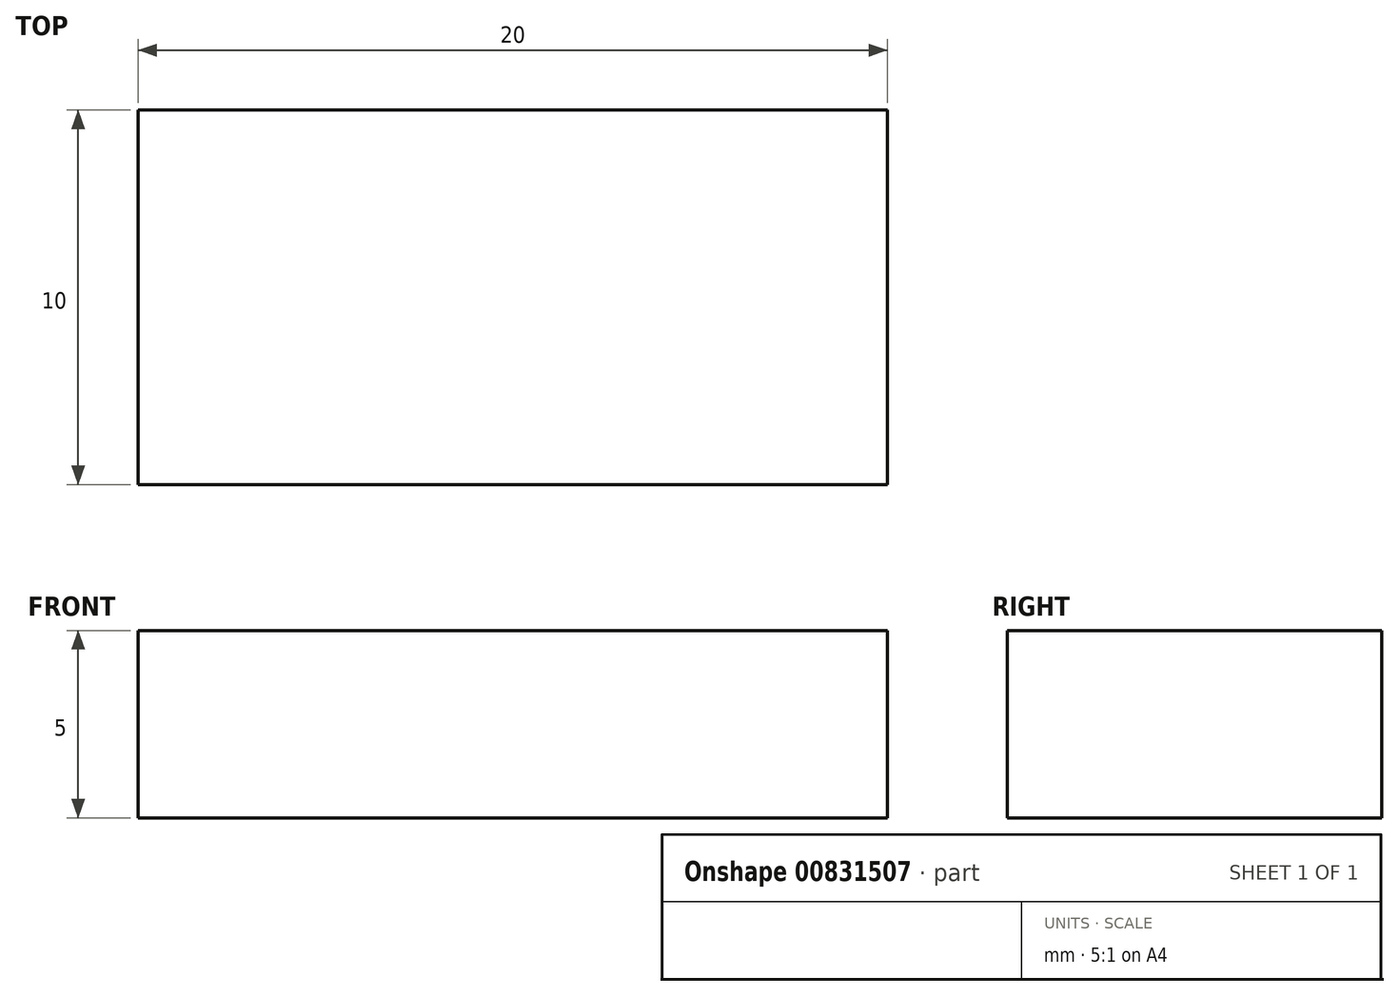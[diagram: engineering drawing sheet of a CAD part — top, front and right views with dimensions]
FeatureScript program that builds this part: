
annotation { "Feature Type Name" : "Feature", "Feature Type Description" : "" }
export const myFeature = defineFeature(function(context is Context, id is Id, definition is map)
    precondition{}
    {
        {
            var Q0;
            Q0=qCreatedBy(makeId("Top.planeOp"),FACE);
            var sketch = newSketch(context, id + "F0", { "sketchPlane" : qUnion([Q0])});
            skLineSegment(sketch, "E0.bottom", {"start": v(-10, 5) * mm, "end": v(10, 5) * mm});
            skLineSegment(sketch, "E0.top", {"start": v(-10, -5) * mm, "end": v(10, -5) * mm});
            skLineSegment(sketch, "E0.left", {"start": v(-10, 5) * mm, "end": v(-10, -5) * mm});
            skLineSegment(sketch, "E0.right", {"start": v(10, 5) * mm, "end": v(10, -5) * mm});
            skSolve(sketch);
        }
        {
            var Q0;
            Q0=makeQuery(id+"F0.imprint","IMPRINT",FACE,{"disambiguationData":[TD([[makeQuery(id+"F0.imprint","IMPRINT",EDGE,{"derivedFrom":sQuery(id+"F0.wireOp",EDGE,"E0.bottom")}),-1.0]])]});
            extrude(context, id + "F1", {"entities" : qUnion([Q0]), "depth" : 5 * mm, "offsetDistance" : 25 * mm});
        }
    });
